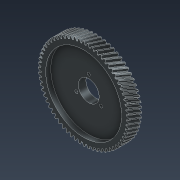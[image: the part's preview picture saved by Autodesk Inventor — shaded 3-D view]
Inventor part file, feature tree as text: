
AUTODESK INVENTOR PART (.ipt)
format: ipt  version: 2022 (Build 260153000, 153)  size: 875,520 bytes
history: native  units: mm (DEFAULTED — no unit token found)
features: sketch x5, extrude x3, plane x3, other x3, hole x1
ambient origin geometry x8: Origin, YZ Plane, XZ Plane, XY Plane, X Axis, Y Axis, Z Axis, Center Point
bodies: Solid1 (feature_tree)
feature tree (15):
  extrude  "Extrusion1"  Depth=20.0mm TaperAngle=0.0deg
  plane  "Work Plane2"
  plane  "Work Plane8"
  plane  "Work Plane9"
  other  "Spur Gear"
  extrude  "Extrusion2"  Depth=10.0mm TaperAngle=0.0deg
  extrude  "Extrusion3"  Depth=0.490874mm TaperAngle=0.0deg
  hole  "Hole1"  [1 undecoded]
  sketch  "Sketch1"  dims[d0=143.892623mm d1=20.0mm d2=0.0mm]
  sketch  "Sketch2"  dims[d3=136.214755mm d4=10.0mm d5=0.0mm]
  other  "Srf1"
  sketch  "Sketch3"  dims[d16=104.0mm d17=0.0mm d34=0.490874mm]
  sketch  "Sketch4"  dims[d39=0.0mm d41=0.0mm]
  sketch  "Sketch5"  dims[d43=104.0mm d46=104.0mm d47=0.0mm d48=0.0mm d49=120.0mm d50=8.0mm d51=0.0mm d52=33.0mm d53=0.0mm d54=0.0mm d55=45.0mm d56=30.0mm d58=360.0deg d60=5.0mm d61=5.0mm d62=4.0mm d63=2.0mm d64=90.0deg d65=5.0mm d66=0.0mm]
  other  "Pitch Diameter"
note: 1 required parameter value undecoded (feature->parameter linkage not recoverable at this tier; creation-order binding heuristic only, values carry confidence <= 0.55)
